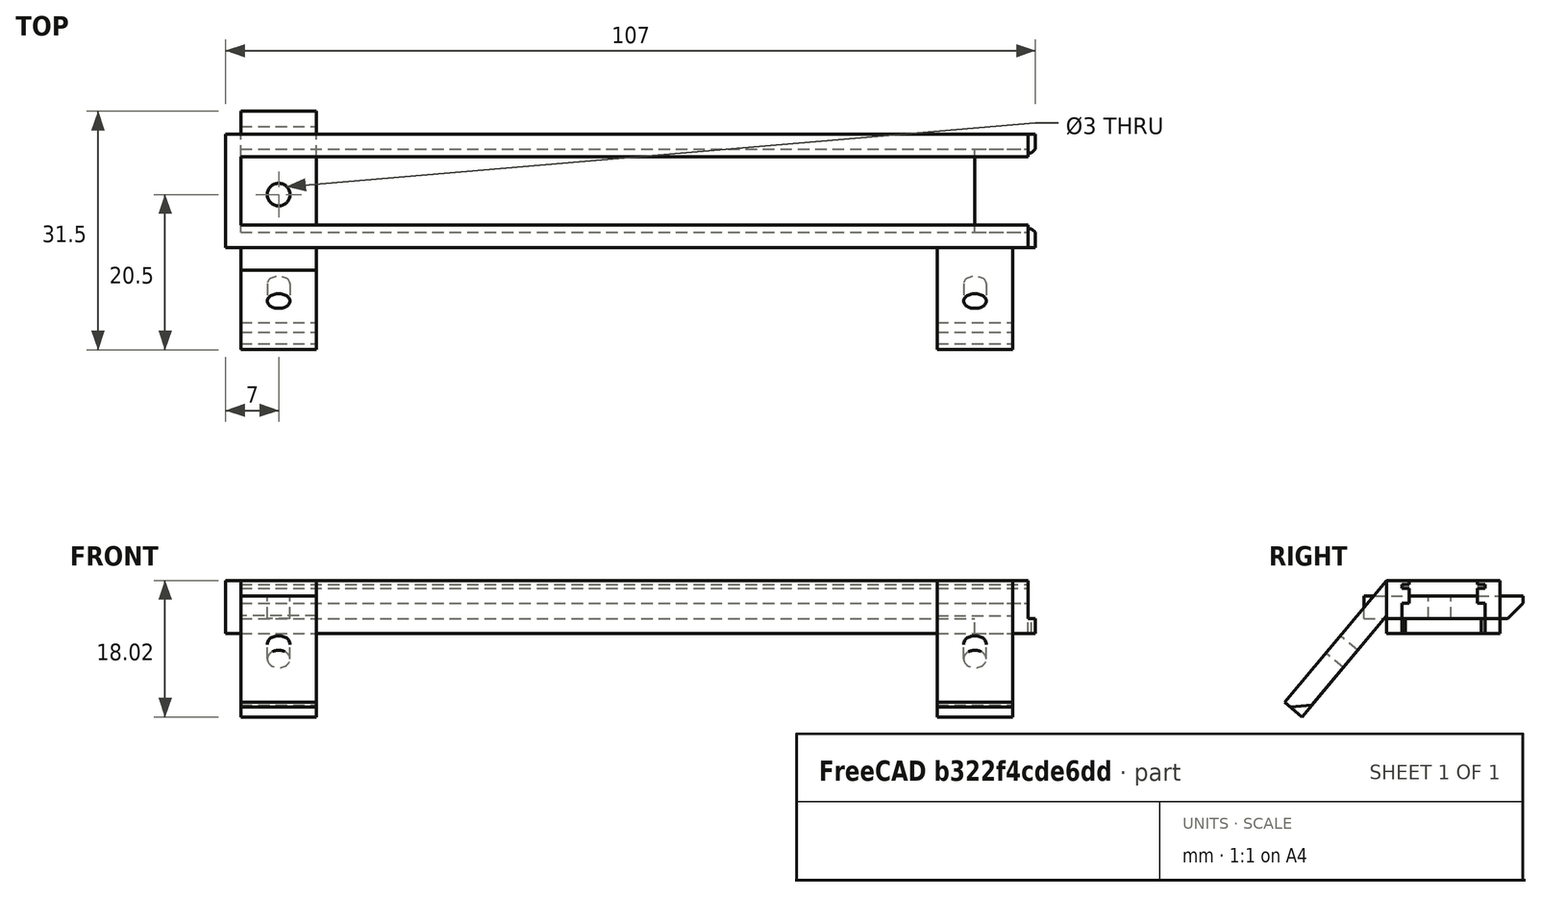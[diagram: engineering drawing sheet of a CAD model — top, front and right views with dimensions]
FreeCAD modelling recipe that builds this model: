
FCSTD DOCUMENT  (FreeCAD 0.18R14555 (Git shallow))
Label: led-mounter
License: All rights reserved
LicenseURL: http://en.wikipedia.org/wiki/All_rights_reserved
objects: Part::Box×8, Part::Cut×5, Part::Chamfer×5, Part::Feature×4, Part::MultiFuse×2, Part::Cylinder×1
note: 25 computed .brp shape members not serialized (recipe doc carries the construction recipe); baked Part::Feature solids carry a one-line shape summary decoded from their .brp

FEATURE [Part::Box] Box  label="led"
  AttacherType = Attacher::AttachEngine3D
  Height = 2
  Length = 104
  Width = 11
FEATURE [Part::Box] Box001  label="filter"
  AttacherType = Attacher::AttachEngine3D
  Height = 0.5
  Length = 104
  Placement = pos=(0,0,4) rot=(0,0,1;0rad)
  Width = 11
FEATURE [Part::Box] Box002  label="cut"
  AttacherType = Attacher::AttachEngine3D
  Height = 5
  Length = 104
  Placement = pos=(0,1,0) rot=(0,0,1;0rad)
  Width = 9
FEATURE [Part::Box] Box003  label="case"
  AttacherType = Attacher::AttachEngine3D
  Height = 7
  Length = 106
  Placement = pos=(-2,-2,-2) rot=(0,0,1;0rad)
  Width = 15
FEATURE [Part::Cut] Cut
  Base = -> Box003
  Tool = -> Box002
FEATURE [Part::Cut] Cut001
  Base = -> Cut
  Tool = -> Box001
FEATURE [Part::Cut] Cut002
  Base = -> Cut001
  Tool = -> Box
FEATURE [Part::Box] Box004  label="Cube"
  AttacherType = Attacher::AttachEngine3D
  Height = 4
  Length = 7
  Placement = pos=(97,0,-2) rot=(0,0,1;0rad)
  Width = 11
FEATURE [Part::Cut] Cut003
  Base = -> Cut002
  Tool = -> Box004
FEATURE [Part::Box] Box005  label="Cube001"
  AttacherType = Attacher::AttachEngine3D
  Height = 2
  Length = 1
  Placement = pos=(104,-2,-2) rot=(0,0,1;0rad)
  Width = 2.5
FEATURE [Part::Box] Box006  label="Cube002"
  AttacherType = Attacher::AttachEngine3D
  Height = 2
  Length = 1
  Placement = pos=(104,10.5,-2) rot=(0,0,1;0rad)
  Width = 2.5
FEATURE [Part::Chamfer] Chamfer
  Base = -> Box005
  Edges = 1 edges r=0.5: [Edge7]
FEATURE [Part::Chamfer] Chamfer001
  Base = -> Box006
  Edges = 1 edges r=0.5: [Edge5]
FEATURE [Part::MultiFuse] Fusion
  Placement = pos=(0,5,0) rot=(0,0,1;0rad)
  Shapes = -> [Cut003,Chamfer,Chamfer001]
FEATURE [Part::Box] Box007  label="Cube003"
  AttacherType = Attacher::AttachEngine3D
  Height = 3
  Length = 10
  Width = 21
FEATURE [Part::Cylinder] Cylinder
  Angle = 360
  AttacherType = Attacher::AttachEngine3D
  Height = 10
  Placement = pos=(5,10,0) rot=(0,0,1;0rad)
  Radius = 1.5
FEATURE [Part::Cut] Cut004
  Base = -> Box007
  Tool = -> Cylinder
FEATURE [Part::Chamfer] Chamfer002
  Base = -> Cut004
  Edges = 1 edges r=2: [Edge11]
FEATURE [Part::Feature] Chamfer002001  label="Chamfer003"
  Placement = pos=(0,-8.2,-13) rot=(1,0,0;0.872665rad)
  shape: bbox 10 x 14.51 x 18.02 mm, 8 faces (baked)
FEATURE [Part::Feature] Chamfer002001001  label="Chamfer004"
  Placement = pos=(92,-8.2,-13) rot=(1,0,0;0.872665rad)
  shape: bbox 10 x 14.51 x 18.02 mm, 8 faces (baked)
FEATURE [Part::MultiFuse] Fusion001
  Shapes = -> [Chamfer002001,Fusion,Chamfer002001001]
FEATURE [Part::Feature] Fusion001001  label="Fusion002"
  shape: bbox 107 x 28.5 x 18.02 mm, 48 faces (baked)
FEATURE [Part::Feature] Fusion001001_solid  label="Fusion002 (Solid)"
  shape: bbox 107 x 28.5 x 18.02 mm, 48 faces (baked)
FEATURE [Part::Chamfer] Chamfer002001002
  Base = -> Fusion001001_solid
  Edges = 1 edges r=2: [Edge70]
FEATURE [Part::Chamfer] Chamfer002001003
  Base = -> Chamfer002001002
  Edges = 1 edges r=2: [Edge76]
